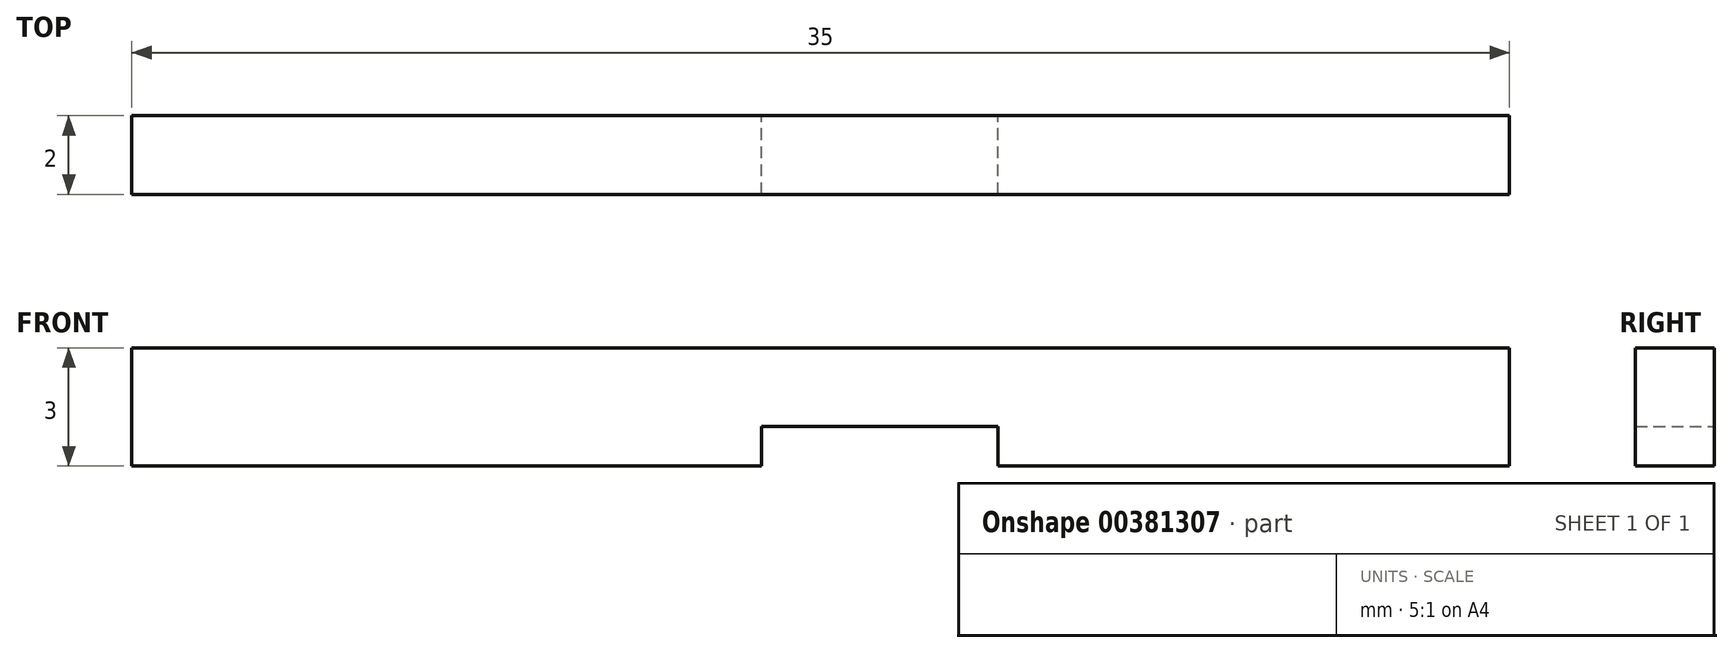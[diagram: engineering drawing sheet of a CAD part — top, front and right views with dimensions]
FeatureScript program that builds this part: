
annotation { "Feature Type Name" : "Feature", "Feature Type Description" : "" }
export const myFeature = defineFeature(function(context is Context, id is Id, definition is map)
    precondition{}
    {
        {
            var Q0;
            Q0=qCreatedBy(makeId("Front.planeOp"),FACE);
            var sketch = newSketch(context, id + "F0", { "sketchPlane" : qUnion([Q0])});
            skLineSegment(sketch, "E0.bottom", {"start": v(17.5, -1.5) * mm, "end": v(4.5, -1.5) * mm});
            skLineSegment(sketch, "E0.top", {"start": v(17.5, 1.5) * mm, "end": v(-17.5, 1.5) * mm});
            skLineSegment(sketch, "E0.left", {"start": v(17.5, -1.5) * mm, "end": v(17.5, 1.5) * mm});
            skLineSegment(sketch, "E0.right", {"start": v(-17.5, -1.5) * mm, "end": v(-17.5, 1.5) * mm});
            skPoint(sketch, "E0.middle", {"position": v(0, 0) * mm});
            skLineSegment(sketch, "E1", {"start": v(-1.5, -0.5) * mm, "end": v(4.5, -0.5) * mm});
            skLineSegment(sketch, "E2", {"start": v(-1.5, -0.5) * mm, "end": v(-1.5, -1.5) * mm});
            skLineSegment(sketch, "E3", {"start": v(4.5, -0.5) * mm, "end": v(4.5, -1.5) * mm});
            skLineSegment(sketch, "E4.trimOffspring", {"start": v(-1.5, -1.5) * mm, "end": v(-17.5, -1.5) * mm});
            skSolve(sketch);
        }
        {
            var Q0;
            Q0 = qSketchRegion(id + "F0", true);
            extrude(context, id + "F1", {"entities" : qUnion([Q0]), "depth" : 2 * mm});
        }
    });
